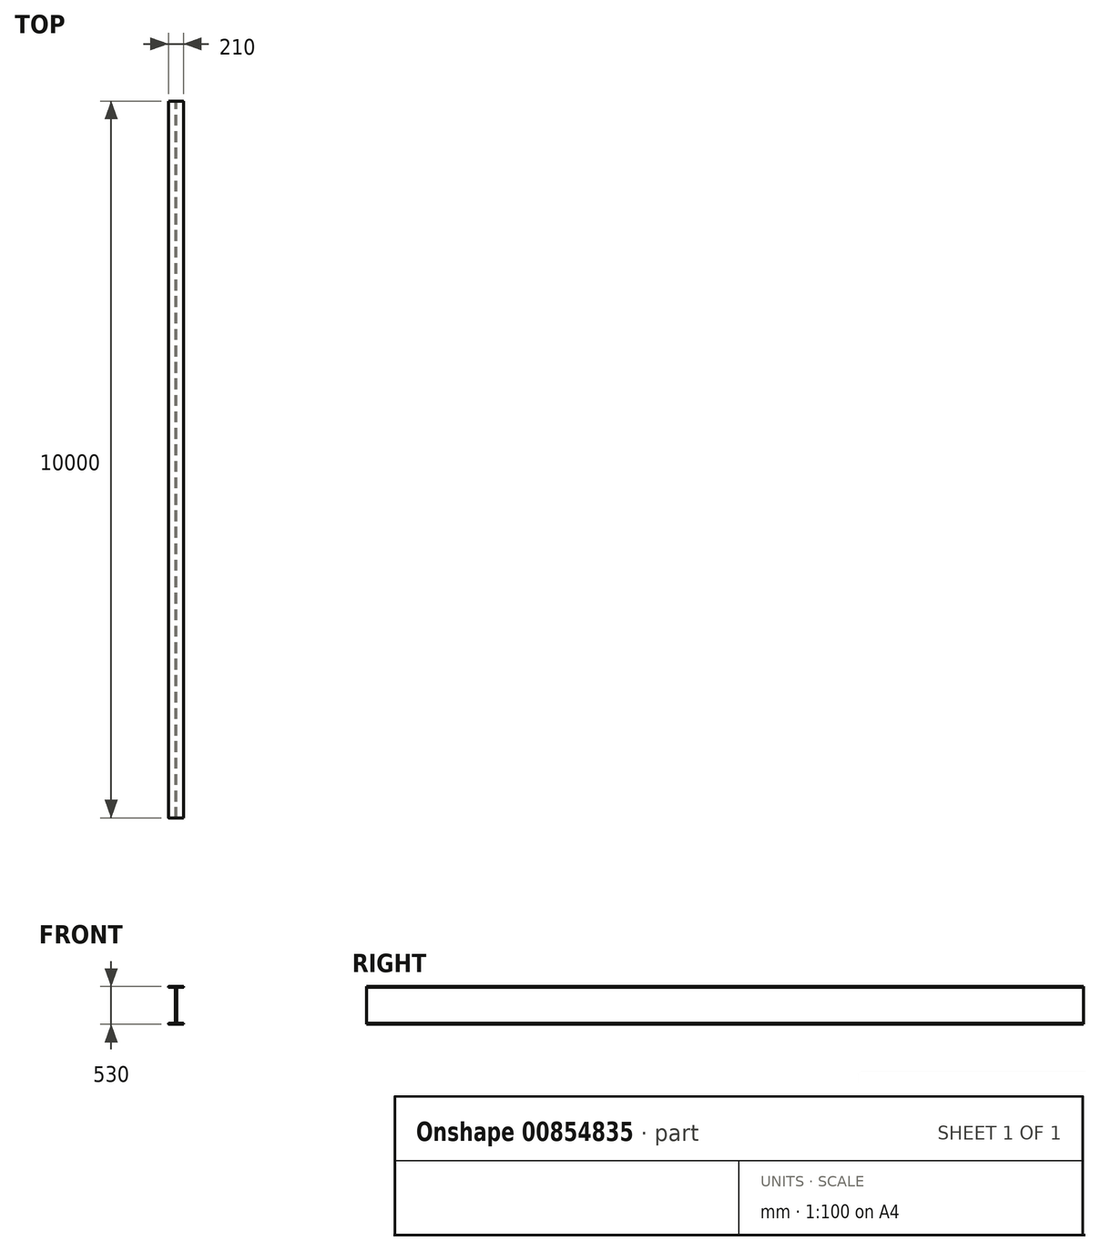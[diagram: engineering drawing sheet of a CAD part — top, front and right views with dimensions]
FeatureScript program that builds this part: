
annotation { "Feature Type Name" : "Feature", "Feature Type Description" : "" }
export const myFeature = defineFeature(function(context is Context, id is Id, definition is map)
    precondition{}
    {
        {
            var Q0;
            Q0=qCreatedBy(makeId("Front.planeOp"),FACE);
            var sketch = newSketch(context, id + "F0", { "sketchPlane" : qUnion([Q0])});
            skLineSegment(sketch, "E0", {"start": v(0, 0) * mm, "end": v(210, 0) * mm});
            skLineSegment(sketch, "E1", {"start": v(210, 0) * mm, "end": v(210, 15) * mm});
            skLineSegment(sketch, "E2", {"start": v(210, 15) * mm, "end": v(112.5, 15) * mm});
            skLineSegment(sketch, "E3", {"start": v(112.5, 15) * mm, "end": v(112.5, 515) * mm});
            skLineSegment(sketch, "E4", {"start": v(112.5, 515) * mm, "end": v(210, 515) * mm});
            skLineSegment(sketch, "E5", {"start": v(210, 515) * mm, "end": v(210, 530) * mm});
            skLineSegment(sketch, "E6", {"start": v(210, 530) * mm, "end": v(0, 530) * mm});
            skLineSegment(sketch, "E7", {"start": v(0, 530) * mm, "end": v(0, 515) * mm});
            skLineSegment(sketch, "E8", {"start": v(0, 515) * mm, "end": v(97.5, 515) * mm});
            skLineSegment(sketch, "E9", {"start": v(97.5, 515) * mm, "end": v(97.5, 15) * mm});
            skLineSegment(sketch, "E10", {"start": v(97.5, 15) * mm, "end": v(0, 15) * mm});
            skLineSegment(sketch, "E11", {"start": v(0, 15) * mm, "end": v(0, 0) * mm});
            skSolve(sketch);
        }
        {
            var Q0;
            Q0 = qSketchRegion(id + "F0", true);
            extrude(context, id + "F1", {"entities" : qUnion([Q0]), "depth" : 10000 * mm, "offsetDistance" : 25 * mm});
        }
        {
            var Q0;
            Q0=makeQuery(id+"F1.opExtrude","SWEPT_EDGE",EDGE,{"disambiguationData":[OSD([sQuery(id+"F0.wireOp",EDGE,"E6"),sQuery(id+"F0.wireOp",EDGE,"E7")])]});
            var Q1;
            Q1=makeQuery(id+"F1.opExtrude","SWEPT_EDGE",EDGE,{"disambiguationData":[OSD([sQuery(id+"F0.wireOp",EDGE,"E7"),sQuery(id+"F0.wireOp",EDGE,"E8")])]});
            var Q2;
            Q2=makeQuery(id+"F1.opExtrude","SWEPT_EDGE",EDGE,{"disambiguationData":[OSD([sQuery(id+"F0.wireOp",EDGE,"E5"),sQuery(id+"F0.wireOp",EDGE,"E6")])]});
            var Q3;
            Q3=makeQuery(id+"F1.opExtrude","SWEPT_EDGE",EDGE,{"disambiguationData":[OSD([sQuery(id+"F0.wireOp",EDGE,"E10"),sQuery(id+"F0.wireOp",EDGE,"E11")])]});
            var Q4;
            Q4=makeQuery(id+"F1.opExtrude","SWEPT_EDGE",EDGE,{"disambiguationData":[OSD([sQuery(id+"F0.wireOp",EDGE,"E0"),sQuery(id+"F0.wireOp",EDGE,"E11")])]});
            var Q5;
            Q5=makeQuery(id+"F1.opExtrude","SWEPT_EDGE",EDGE,{"disambiguationData":[OSD([sQuery(id+"F0.wireOp",EDGE,"E1"),sQuery(id+"F0.wireOp",EDGE,"E2")])]});
            var Q6;
            Q6=makeQuery(id+"F1.opExtrude","SWEPT_EDGE",EDGE,{"disambiguationData":[OSD([sQuery(id+"F0.wireOp",EDGE,"E0"),sQuery(id+"F0.wireOp",EDGE,"E1")])]});
            var Q7;
            Q7=makeQuery(id+"F1.opExtrude","SWEPT_EDGE",EDGE,{"disambiguationData":[OSD([sQuery(id+"F0.wireOp",EDGE,"E4"),sQuery(id+"F0.wireOp",EDGE,"E5")])]});
            var Q8;
            Q8=makeQuery(id+"F1.opExtrude","SWEPT_EDGE",EDGE,{"disambiguationData":[OSD([sQuery(id+"F0.wireOp",EDGE,"E2"),sQuery(id+"F0.wireOp",EDGE,"E3")])]});
            var Q9;
            Q9=makeQuery(id+"F1.opExtrude","SWEPT_EDGE",EDGE,{"disambiguationData":[OSD([sQuery(id+"F0.wireOp",EDGE,"E9"),sQuery(id+"F0.wireOp",EDGE,"E10")])]});
            var Q10;
            Q10=makeQuery(id+"F1.opExtrude","SWEPT_EDGE",EDGE,{"disambiguationData":[OSD([sQuery(id+"F0.wireOp",EDGE,"E8"),sQuery(id+"F0.wireOp",EDGE,"E9")])]});
            var Q11;
            Q11=makeQuery(id+"F1.opExtrude","SWEPT_EDGE",EDGE,{"disambiguationData":[OSD([sQuery(id+"F0.wireOp",EDGE,"E3"),sQuery(id+"F0.wireOp",EDGE,"E4")])]});
            fillet(context, id + "F2", {"entities" : qUnion([Q0, Q1, Q2, Q3, Q4, Q5, Q6, Q7, Q8, Q9, Q10, Q11]), "radius" : 5 * mm, "tangentPropagation" : true, "allowEdgeOverflow" : false});
        }
    });
